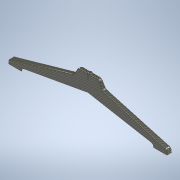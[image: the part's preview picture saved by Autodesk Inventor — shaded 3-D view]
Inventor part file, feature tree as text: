
AUTODESK INVENTOR PART (.ipt)
format: ipt  version: 2022 (Build 260153000, 153)  size: 500,736 bytes
history: native  units: mm
features: sketch x4, other x3, extrude x2, fillet x2, mirror x1, shell x1, hole x1
ambient origin geometry x8: Origin, YZ Plane, XZ Plane, XY Plane, X Axis, Y Axis, Z Axis, Center Point
bodies: Body1 (feature_tree)
feature tree (14):
  other  "Těleso1"
  sketch  "Náčrt1"
  extrude  "Vysunutí1"  Depth=10.0mm
  extrude  "Vysunutí2"  Depth=92.0mm
  mirror  "Zrcadlit1"
  fillet  "Zaoblení1"  Radius=240.0mm
  shell  "Skořepina1"  Thickness=0.0mm
  other  "Rotace1"
  fillet  "Zaoblení2"  Radius=10.0mm
  hole  "Díra1"  [1 undecoded]
  sketch  "Náčrt2"
  sketch  "Náčrt4"
  other  "Obrázek1"
  sketch  "Náčrt5"
note: 1 required parameter value undecoded (feature->parameter linkage not recoverable at this tier; creation-order binding heuristic only, values carry confidence <= 0.55)
